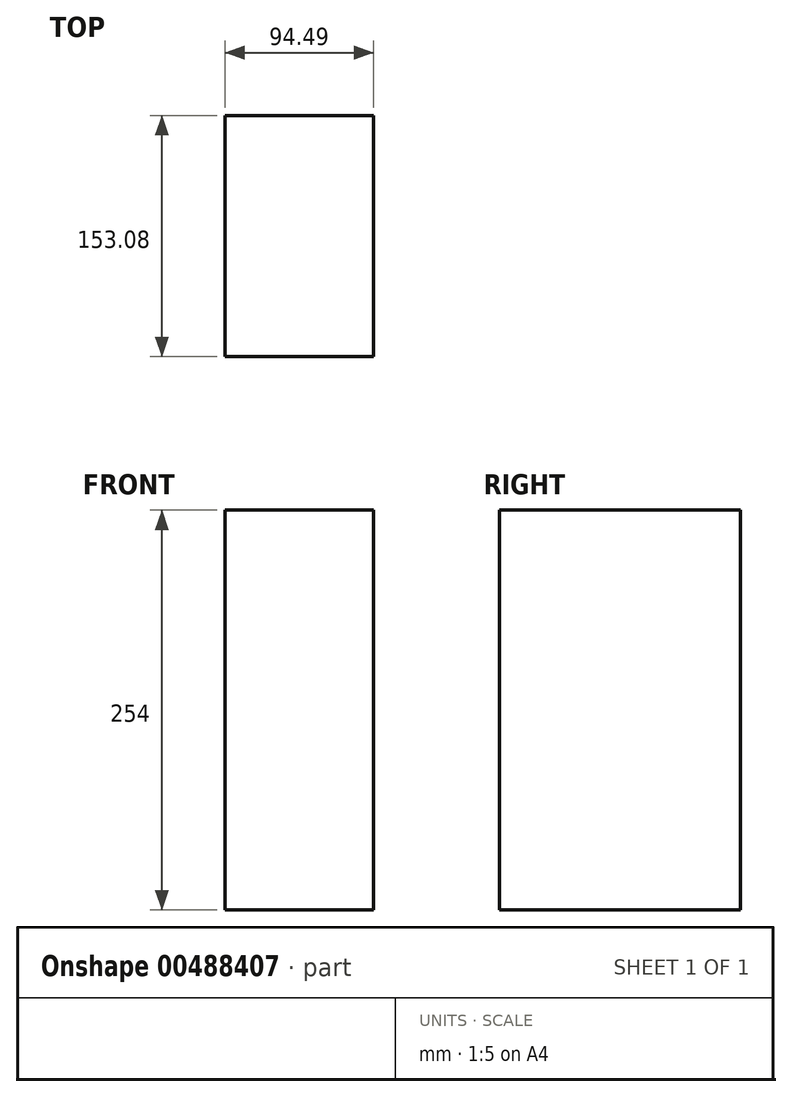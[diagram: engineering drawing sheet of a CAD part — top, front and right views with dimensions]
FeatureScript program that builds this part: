
annotation { "Feature Type Name" : "Feature", "Feature Type Description" : "" }
export const myFeature = defineFeature(function(context is Context, id is Id, definition is map)
    precondition{}
    {
        {
            var Q0;
            Q0=qCreatedBy(makeId("Top.planeOp"),FACE);
            var sketch = newSketch(context, id + "F0", { "sketchPlane" : qUnion([Q0])});
            skLineSegment(sketch, "E0.bottom", {"start": v(-48.8, 76.66) * mm, "end": v(45.69, 76.66) * mm});
            skLineSegment(sketch, "E0.top", {"start": v(-48.8, -76.42) * mm, "end": v(45.69, -76.42) * mm});
            skLineSegment(sketch, "E0.left", {"start": v(-48.8, 76.66) * mm, "end": v(-48.8, -76.42) * mm});
            skLineSegment(sketch, "E0.right", {"start": v(45.69, 76.66) * mm, "end": v(45.69, -76.42) * mm});
            skSolve(sketch);
        }
        {
            var Q0;
            Q0 = qSketchRegion(id + "F0", true);
            extrude(context, id + "F1", {"entities" : qUnion([Q0]), "oppositeDirection" : true, "depth" : 254 * mm});
        }
    });
